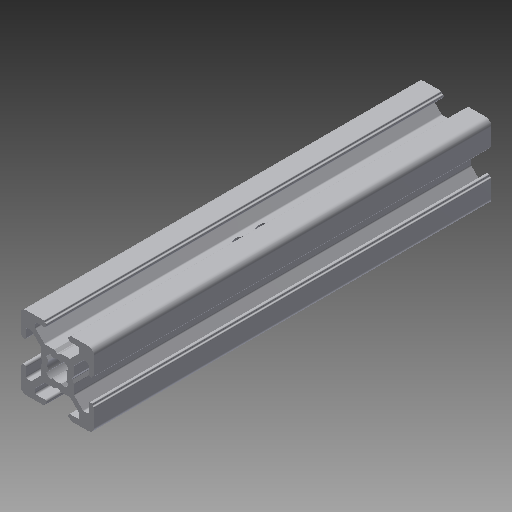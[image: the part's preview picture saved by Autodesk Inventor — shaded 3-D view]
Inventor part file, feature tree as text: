
AUTODESK INVENTOR PART (.ipt)
format: ipt  version: 2017 (Build 210142000, 142)  size: 415,232 bytes
history: native  units: in
note: dims shown in document units (in); Inventor stores cm internally (conversion verified against a paired STEP export)
features: other x3, sketch x2, extrude x1, hole x1, mirror x1
ambient origin geometry x8: Origin, YZ Plane, XZ Plane, XY Plane, X Axis, Y Axis, Z Axis, Center Point
bodies: Solid1 (feature_tree)
feature tree (8):
  other  "Blocks"
  extrude  "Extrusion1"  Depth=2.0in
  hole  "Hole1"  [1 undecoded]
  mirror  "Mirror1"
  sketch  "Sketch1"  dims[d1=0.0in d5=2.0in]
  other  "20x20"
  sketch  "Sketch3"  dims[d6=0.187in d7=0.75in d8=0.375in d9=0.25in d10=0.5635in d11=1.0in d12=0.8108in d13=1.0in d14=1.0in]
  other  "20x20:1"
note: 1 required parameter value undecoded (feature->parameter linkage not recoverable at this tier; creation-order binding heuristic only, values carry confidence <= 0.55)
